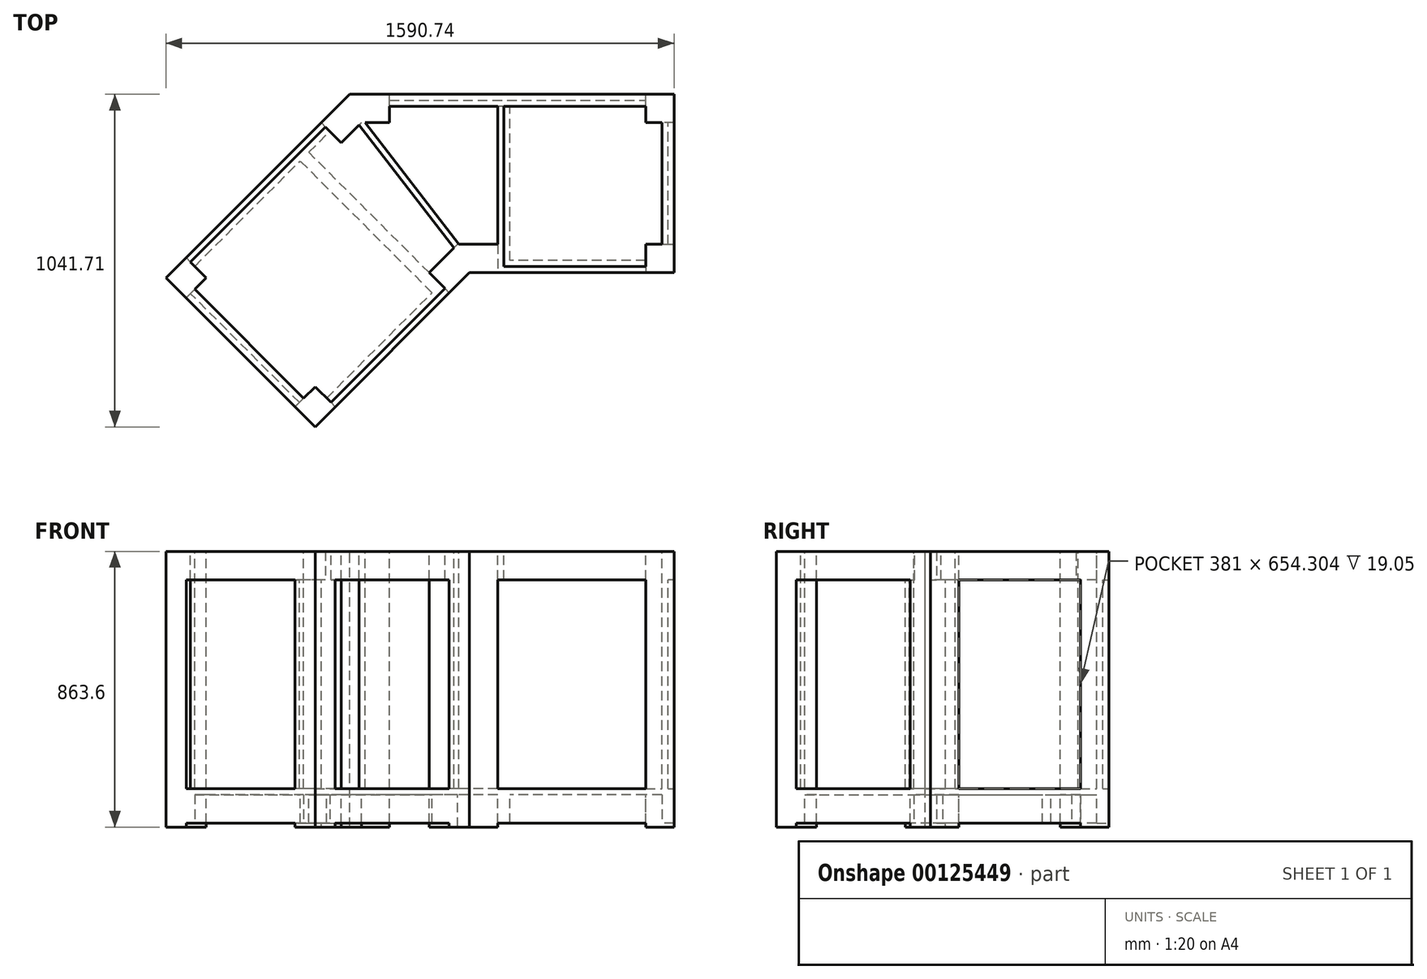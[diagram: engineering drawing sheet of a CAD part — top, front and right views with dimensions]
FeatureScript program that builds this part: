
annotation { "Feature Type Name" : "Feature", "Feature Type Description" : "" }
export const myFeature = defineFeature(function(context is Context, id is Id, definition is map)
    precondition{}
    {
        {
            var Q0;
            Q0=qCreatedBy(makeId("Top.planeOp"),FACE);
            var sketch = newSketch(context, id + "F0", { "sketchPlane" : qUnion([Q0])});
            skLineSegment(sketch, "E0", {"start": v(0, 0) * mm, "end": v(1016, 0) * mm, "construction": true});
            skLineSegment(sketch, "E1", {"start": v(-574.74, -574.74) * mm, "end": v(0, 0) * mm, "construction": true});
            skLineSegment(sketch, "E2.bottom", {"start": v(-88.9, -88.9) * mm, "end": v(-26.04, -26.04) * mm});
            skLineSegment(sketch, "E2.top", {"start": v(-26.04, -151.76) * mm, "end": v(36.82, -88.9) * mm});
            skLineSegment(sketch, "E2.left", {"start": v(-88.9, -88.9) * mm, "end": v(-26.04, -151.76) * mm});
            skLineSegment(sketch, "E3.bottom", {"start": v(36.82, 0) * mm, "end": v(125.72, 0) * mm});
            skLineSegment(sketch, "E3.top", {"start": v(36.82, -88.9) * mm, "end": v(125.72, -88.9) * mm});
            skLineSegment(sketch, "E3.right", {"start": v(125.72, 0) * mm, "end": v(125.72, -88.9) * mm});
            skLineSegment(sketch, "E4.bottom", {"start": v(-574.74, -574.74) * mm, "end": v(-511.87, -511.87) * mm});
            skLineSegment(sketch, "E4.top", {"start": v(-511.87, -637.6) * mm, "end": v(-449.01, -574.74) * mm});
            skLineSegment(sketch, "E4.left", {"start": v(-574.74, -574.74) * mm, "end": v(-511.87, -637.6) * mm});
            skLineSegment(sketch, "E4.right", {"start": v(-511.87, -511.87) * mm, "end": v(-449.01, -574.74) * mm});
            skLineSegment(sketch, "E5.bottom", {"start": v(927.1, 0) * mm, "end": v(1016, 0) * mm});
            skLineSegment(sketch, "E5.top", {"start": v(927.1, -88.9) * mm, "end": v(1016, -88.9) * mm});
            skLineSegment(sketch, "E5.left", {"start": v(927.1, 0) * mm, "end": v(927.1, -88.9) * mm});
            skLineSegment(sketch, "E5.right", {"start": v(1016, 0) * mm, "end": v(1016, -88.9) * mm});
            skLineSegment(sketch, "E6", {"start": v(-26.04, -26.04) * mm, "end": v(0, 0) * mm});
            skLineSegment(sketch, "E7", {"start": v(36.82, 0) * mm, "end": v(0, 0) * mm});
            skLineSegment(sketch, "E8", {"start": v(-574.74, -574.74) * mm, "end": v(-107.76, -1041.7) * mm, "construction": true});
            skLineSegment(sketch, "E9", {"start": v(-107.76, -1041.7) * mm, "end": v(375.15, -558.8) * mm, "construction": true});
            skLineSegment(sketch, "E10", {"start": v(375.15, -558.8) * mm, "end": v(1016, -558.8) * mm, "construction": true});
            skLineSegment(sketch, "E11", {"start": v(1016, -558.8) * mm, "end": v(1016, 0) * mm, "construction": true});
            skLineSegment(sketch, "E12.bottom", {"start": v(-107.76, -1041.7) * mm, "end": v(-44.9, -978.85) * mm});
            skLineSegment(sketch, "E12.top", {"start": v(-170.62, -978.85) * mm, "end": v(-107.76, -915.99) * mm});
            skLineSegment(sketch, "E12.left", {"start": v(-107.76, -1041.7) * mm, "end": v(-170.62, -978.85) * mm});
            skLineSegment(sketch, "E12.right", {"start": v(-44.9, -978.85) * mm, "end": v(-107.76, -915.99) * mm});
            skLineSegment(sketch, "E13.bottom", {"start": v(1016, -558.8) * mm, "end": v(927.1, -558.8) * mm});
            skLineSegment(sketch, "E13.top", {"start": v(1016, -469.9) * mm, "end": v(927.1, -469.9) * mm});
            skLineSegment(sketch, "E13.left", {"start": v(1016, -558.8) * mm, "end": v(1016, -469.9) * mm});
            skLineSegment(sketch, "E13.right", {"start": v(927.1, -558.8) * mm, "end": v(927.1, -469.9) * mm});
            skLineSegment(sketch, "E14.bottom", {"start": v(375.15, -558.8) * mm, "end": v(464.05, -558.8) * mm});
            skLineSegment(sketch, "E14.top", {"start": v(375.15, -469.9) * mm, "end": v(464.05, -469.9) * mm});
            skLineSegment(sketch, "E14.right", {"start": v(464.05, -558.8) * mm, "end": v(464.05, -469.9) * mm});
            skLineSegment(sketch, "E15.bottom", {"start": v(375.15, -558.8) * mm, "end": v(312.28, -621.66) * mm});
            skLineSegment(sketch, "E15.top", {"start": v(312.28, -495.94) * mm, "end": v(249.42, -558.8) * mm});
            skLineSegment(sketch, "E15.right", {"start": v(312.28, -621.66) * mm, "end": v(249.42, -558.8) * mm});
            skLineSegment(sketch, "E16", {"start": v(312.28, -495.94) * mm, "end": v(338.32, -469.9) * mm});
            skLineSegment(sketch, "E17", {"start": v(375.15, -469.9) * mm, "end": v(338.32, -469.9) * mm});
            skSolve(sketch);
        }
        {
            var Q0;
            Q0=makeQuery(id+"F0.imprint","IMPRINT",FACE,{"disambiguationData":[TD([[makeQuery(id+"F0.imprint","IMPRINT",EDGE,{"derivedFrom":sQuery(id+"F0.wireOp",EDGE,"E2.bottom")}),-1.0]])]});
            var Q1;
            Q1=makeQuery(id+"F0.imprint","IMPRINT",FACE,{"disambiguationData":[TD([[makeQuery(id+"F0.imprint","IMPRINT",EDGE,{"derivedFrom":sQuery(id+"F0.wireOp",EDGE,"E3.bottom")}),-1.0]])]});
            var Q2;
            Q2=makeQuery(id+"F0.imprint","IMPRINT",FACE,{"disambiguationData":[TD([[makeQuery(id+"F0.imprint","IMPRINT",EDGE,{"derivedFrom":sQuery(id+"F0.wireOp",EDGE,"E5.bottom")}),-1.0]])]});
            var Q3;
            Q3=makeQuery(id+"F0.imprint","IMPRINT",FACE,{"disambiguationData":[TD([[makeQuery(id+"F0.imprint","IMPRINT",EDGE,{"derivedFrom":sQuery(id+"F0.wireOp",EDGE,"E4.bottom")}),-1.0]])]});
            var Q4;
            Q4=makeQuery(id+"F0.imprint","IMPRINT",FACE,{"disambiguationData":[TD([[makeQuery(id+"F0.imprint","IMPRINT",EDGE,{"derivedFrom":sQuery(id+"F0.wireOp",EDGE,"E12.bottom")}),1.0]])]});
            var Q5;
            Q5=makeQuery(id+"F0.imprint","IMPRINT",FACE,{"disambiguationData":[TD([[makeQuery(id+"F0.imprint","IMPRINT",EDGE,{"derivedFrom":sQuery(id+"F0.wireOp",EDGE,"E14.bottom")}),1.0]])]});
            var Q6;
            Q6=makeQuery(id+"F0.imprint","IMPRINT",FACE,{"disambiguationData":[TD([[makeQuery(id+"F0.imprint","IMPRINT",EDGE,{"derivedFrom":sQuery(id+"F0.wireOp",EDGE,"E13.bottom")}),-1.0]])]});
            extrude(context, id + "F1", {"entities" : qUnion([Q0, Q1, Q2, Q3, Q4, Q5, Q6]), "oppositeDirection" : true, "depth" : 863.6 * mm});
        }
        {
            var Q0;
            Q0=qCreatedBy(makeId("Top.planeOp"),FACE);
            var sketch = newSketch(context, id + "F2", { "sketchPlane" : qUnion([Q0])});
            skLineSegment(sketch, "E18.bottom", {"start": v(0, 0) * mm, "end": v(1016, 0) * mm});
            skLineSegment(sketch, "E19.MirrorCS", {"start": v(0, 0) * mm, "end": v(-574.74, -574.74) * mm});
            skPoint(sketch, "E20.orphan", {"position": v(0, -25.4) * mm});
            skPoint(sketch, "E21.orphan", {"position": v(8.69, -23.87) * mm});
            skLineSegment(sketch, "E22.bottom", {"start": v(-107.76, -1041.7) * mm, "end": v(375.15, -558.8) * mm});
            skLineSegment(sketch, "E23.bottom", {"start": v(1016, -558.8) * mm, "end": v(375.15, -558.8) * mm});
            skLineSegment(sketch, "E24", {"start": v(-574.74, -574.74) * mm, "end": v(-107.76, -1041.7) * mm});
            skLineSegment(sketch, "E25", {"start": v(1016, 0) * mm, "end": v(1016, -558.8) * mm});
            skLineSegment(sketch, "E26.1", {"start": v(-107.76, -1014.77) * mm, "end": v(367.26, -539.75) * mm});
            skLineSegment(sketch, "E26.2", {"start": v(996.95, -539.75) * mm, "end": v(483.1, -539.75) * mm});
            skLineSegment(sketch, "E26.3", {"start": v(-547.8, -574.74) * mm, "end": v(-107.76, -1014.77) * mm});
            skLineSegment(sketch, "E26.4", {"start": v(996.95, -19.05) * mm, "end": v(996.95, -539.75) * mm});
            skLineSegment(sketch, "E26.5", {"start": v(7.9, -19.05) * mm, "end": v(464.05, -19.05) * mm});
            skLineSegment(sketch, "E27.MirrorCS", {"start": v(483.1, -19.05) * mm, "end": v(483.1, -539.75) * mm});
            skLineSegment(sketch, "E28.MirrorCS", {"start": v(464.05, -19.05) * mm, "end": v(464.05, -539.75) * mm});
            skLineSegment(sketch, "E29.trimOffspring", {"start": v(7.9, -19.05) * mm, "end": v(-547.8, -574.74) * mm});
            skLineSegment(sketch, "E30.trimOffspring", {"start": v(483.1, -19.05) * mm, "end": v(996.95, -19.05) * mm});
            skLineSegment(sketch, "E31.trimOffspring", {"start": v(464.05, -539.75) * mm, "end": v(367.26, -539.75) * mm});
            skSolve(sketch);
        }
        {
            var Q0;
            Q0=makeQuery(id+"F2.imprint","IMPRINT",FACE,{"disambiguationData":[TD([[makeQuery(id+"F2.imprint","IMPRINT",EDGE,{"derivedFrom":sQuery(id+"F2.wireOp",EDGE,"E18.bottom")}),-1.0]])]});
            extrude(context, id + "F3", {"entities" : qUnion([Q0]), "oppositeDirection" : true, "depth" : 88.9 * mm});
        }
        {
            var Q0;
            Q0=makeQuery(id+"F1.opExtrude","SWEPT_BODY",BODY,{"disambiguationData":[OSD([sQuery(id+"F0.wireOp",EDGE,"E3.bottom"),sQuery(id+"F0.wireOp",EDGE,"E3.top"),sQuery(id+"F0.wireOp",EDGE,"E3.left"),sQuery(id+"F0.wireOp",EDGE,"E3.right")])]});
            var Q1;
            Q1=makeQuery(id+"F3.opExtrude","SWEPT_BODY",BODY,{"disambiguationData":[OSD([sQuery(id+"F2.wireOp",EDGE,"E18.bottom"),sQuery(id+"F2.wireOp",EDGE,"E18.top"),sQuery(id+"F2.wireOp",EDGE,"E18.right"),sQuery(id+"F2.wireOp",EDGE,"85fa7ddf-3c67-48b7-9abf-f146a85abdcc0.MirrorCS"),sQuery(id+"F2.wireOp",EDGE,"E19.MirrorCS"),sQuery(id+"F2.wireOp",EDGE,"1de45453-a286-46f3-bc31-238e124999270.MirrorCS")])]});
            var Q2;
            Q2=makeQuery(id+"F1.opExtrude","SWEPT_BODY",BODY,{"disambiguationData":[OSD([sQuery(id+"F0.wireOp",EDGE,"E5.bottom"),sQuery(id+"F0.wireOp",EDGE,"E5.top"),sQuery(id+"F0.wireOp",EDGE,"E5.left"),sQuery(id+"F0.wireOp",EDGE,"E5.right")])]});
            var Q3;
            Q3=makeQuery(id+"F1.opExtrude","SWEPT_BODY",BODY,{"disambiguationData":[OSD([sQuery(id+"F0.wireOp",EDGE,"E4.bottom"),sQuery(id+"F0.wireOp",EDGE,"E4.top"),sQuery(id+"F0.wireOp",EDGE,"E4.left"),sQuery(id+"F0.wireOp",EDGE,"E4.right")])]});
            var Q4;
            Q4=makeQuery(id+"F1.opExtrude","SWEPT_BODY",BODY,{"disambiguationData":[OSD([sQuery(id+"F0.wireOp",EDGE,"E12.bottom"),sQuery(id+"F0.wireOp",EDGE,"E12.top"),sQuery(id+"F0.wireOp",EDGE,"E12.left"),sQuery(id+"F0.wireOp",EDGE,"E12.right")])]});
            var Q5;
            Q5=makeQuery(id+"F1.opExtrude","SWEPT_BODY",BODY,{"disambiguationData":[OSD([sQuery(id+"F0.wireOp",EDGE,"E14.bottom"),sQuery(id+"F0.wireOp",EDGE,"E14.top"),sQuery(id+"F0.wireOp",EDGE,"E14.right"),sQuery(id+"F0.wireOp",EDGE,"E15.bottom"),sQuery(id+"F0.wireOp",EDGE,"E15.top"),sQuery(id+"F0.wireOp",EDGE,"E15.right"),sQuery(id+"F0.wireOp",EDGE,"E16"),sQuery(id+"F0.wireOp",EDGE,"E17")])]});
            var Q6;
            Q6=makeQuery(id+"F1.opExtrude","SWEPT_BODY",BODY,{"disambiguationData":[OSD([sQuery(id+"F0.wireOp",EDGE,"E13.bottom"),sQuery(id+"F0.wireOp",EDGE,"E13.top"),sQuery(id+"F0.wireOp",EDGE,"E13.left"),sQuery(id+"F0.wireOp",EDGE,"E13.right")])]});
            booleanBodies(context, id + "F4", {"operationType" : BooleanOperationType.UNION, "tools" : qUnion([Q0, Q1, Q2, Q3, Q4, Q5, Q6])});
        }
        {
            var Q0;
            Q0=qCreatedBy(makeId("Top.planeOp"),FACE);
            cPlane(context, id + "F5", {"entities" : qUnion([Q0]), "cplaneType" : CPlaneType.OFFSET, "offset" : 762 * mm, "oppositeDirection" : true, "width" : 152.4 * mm, "height" : 152.4 * mm});
        }
        {
            var Q0;
            Q0=qCreatedBy(id+"F5.planeOp",FACE);
            var sketch = newSketch(context, id + "F6", { "sketchPlane" : qUnion([Q0])});
            skLineSegment(sketch, "E32.bottom", {"start": v(0, 0) * mm, "end": v(1016, 0) * mm});
            skLineSegment(sketch, "E32.top", {"start": v(375.15, -558.8) * mm, "end": v(1016, -558.8) * mm});
            skLineSegment(sketch, "E32.right", {"start": v(1016, 0) * mm, "end": v(1016, -558.8) * mm});
            skLineSegment(sketch, "E33.MirrorCS", {"start": v(375.15, -558.8) * mm, "end": v(-107.76, -1041.7) * mm});
            skLineSegment(sketch, "E34.MirrorCS", {"start": v(0, 0) * mm, "end": v(-574.74, -574.74) * mm});
            skLineSegment(sketch, "E35.MirrorCS", {"start": v(-574.74, -574.74) * mm, "end": v(-107.76, -1041.7) * mm});
            skPoint(sketch, "E36.orphan", {"position": v(275.74, -558.8) * mm});
            skPoint(sketch, "E37.orphan", {"position": v(375.15, -558.8) * mm});
            skLineSegment(sketch, "E38.0", {"start": v(15.78, -38.1) * mm, "end": v(-127.75, -181.63) * mm});
            skLineSegment(sketch, "E38.1", {"start": v(359.37, -520.7) * mm, "end": v(285.34, -594.72) * mm});
            skLineSegment(sketch, "E38.2", {"start": v(359.37, -520.7) * mm, "end": v(464.05, -520.7) * mm});
            skLineSegment(sketch, "E38.3", {"start": v(-520.85, -574.74) * mm, "end": v(-107.76, -987.83) * mm});
            skLineSegment(sketch, "E38.4", {"start": v(977.9, -38.1) * mm, "end": v(977.9, -520.7) * mm});
            skLineSegment(sketch, "E38.5", {"start": v(15.78, -38.1) * mm, "end": v(464.05, -38.1) * mm});
            skLineSegment(sketch, "E39", {"start": v(-127.75, -181.63) * mm, "end": v(285.34, -594.72) * mm});
            skLineSegment(sketch, "E40.0", {"start": v(-154.69, -208.57) * mm, "end": v(258.4, -621.66) * mm});
            skLineSegment(sketch, "E41.trimOffspring", {"start": v(-154.69, -208.57) * mm, "end": v(-520.85, -574.74) * mm});
            skLineSegment(sketch, "E42.trimOffspring", {"start": v(258.4, -621.66) * mm, "end": v(-107.76, -987.83) * mm});
            skLineSegment(sketch, "E43.MirrorCS", {"start": v(464.05, -38.1) * mm, "end": v(464.05, -520.7) * mm});
            skLineSegment(sketch, "E44.MirrorCS", {"start": v(502.15, -38.1) * mm, "end": v(502.15, -520.7) * mm});
            skLineSegment(sketch, "E45.trimOffspring", {"start": v(502.15, -38.1) * mm, "end": v(977.9, -38.1) * mm});
            skLineSegment(sketch, "E46.trimOffspring", {"start": v(502.15, -520.7) * mm, "end": v(977.9, -520.7) * mm});
            skSolve(sketch);
        }
        {
            var Q0;
            Q0=makeQuery(id+"F6.imprint","IMPRINT",FACE,{"disambiguationData":[TD([[makeQuery(id+"F6.imprint","IMPRINT",EDGE,{"derivedFrom":sQuery(id+"F6.wireOp",EDGE,"E32.bottom")}),-1.0]])]});
            extrude(context, id + "F7", {"entities" : qUnion([Q0]), "operationType" : NewBodyOperationType.ADD, "oppositeDirection" : true, "depth" : 88.9 * mm});
        }
        {
            var Q0;
            {var subQ0=sQuery(id+"F6.wireOp",EDGE,"E35.MirrorCS");var subQ1=sQuery(id+"F6.wireOp",EDGE,"E38.3");Q0=makeQuery(id+"F7.boolean.opBoolean","SPLIT",FACE,{"disambiguationData":[TD([makeQuery(id+"F1.opExtrude","SWEPT_FACE",FACE,{"disambiguationData":[OSD([sQuery(id+"F0.wireOp",EDGE,"E4.top")])]})])],"derivedFrom":makeQuery(id+"F7.opExtrude","CAP_FACE",FACE,{"disambiguationData":[OSD([sQuery(id+"F6.wireOp",EDGE,"E32.bottom"),sQuery(id+"F6.wireOp",EDGE,"E32.top"),sQuery(id+"F6.wireOp",EDGE,"E32.right"),sQuery(id+"F6.wireOp",EDGE,"E33.MirrorCS"),sQuery(id+"F6.wireOp",EDGE,"E34.MirrorCS"),subQ0,sQuery(id+"F6.wireOp",EDGE,"E38.0"),sQuery(id+"F6.wireOp",EDGE,"E38.1"),sQuery(id+"F6.wireOp",EDGE,"E38.2"),subQ1,sQuery(id+"F6.wireOp",EDGE,"E38.4"),sQuery(id+"F6.wireOp",EDGE,"E38.5"),sQuery(id+"F6.wireOp",EDGE,"E39"),sQuery(id+"F6.wireOp",EDGE,"E40.0"),sQuery(id+"F6.wireOp",EDGE,"E41.trimOffspring"),sQuery(id+"F6.wireOp",EDGE,"E42.trimOffspring"),sQuery(id+"F6.wireOp",EDGE,"E43.MirrorCS"),sQuery(id+"F6.wireOp",EDGE,"E44.MirrorCS"),sQuery(id+"F6.wireOp",EDGE,"E45.trimOffspring"),sQuery(id+"F6.wireOp",EDGE,"E46.trimOffspring")])],"isStart":true})});}
            var sketch = newSketch(context, id + "F8", { "sketchPlane" : qUnion([Q0])});
            skLineSegment(sketch, "E47", {"start": v(-107.76, -1041.7) * mm, "end": v(375.15, -558.8) * mm});
            skLineSegment(sketch, "E48", {"start": v(375.15, -558.8) * mm, "end": v(1016, -558.8) * mm});
            skLineSegment(sketch, "E49", {"start": v(1016, -558.8) * mm, "end": v(1016, 0) * mm});
            skLineSegment(sketch, "E50", {"start": v(1016, 0) * mm, "end": v(0, 0) * mm});
            skLineSegment(sketch, "E51", {"start": v(0, 0) * mm, "end": v(-574.74, -574.74) * mm});
            skLineSegment(sketch, "E52", {"start": v(-574.74, -574.74) * mm, "end": v(-107.76, -1041.7) * mm});
            skSolve(sketch);
        }
        {
            var Q0;
            Q0 = qSketchRegion(id + "F8", true);
            extrude(context, id + "F9", {"entities" : qUnion([Q0]), "operationType" : NewBodyOperationType.ADD, "depth" : 18.8 * mm, "hasSecondDirection" : true, "secondDirectionOppositeDirection" : true, "secondDirectionDepth" : 0.25 * mm});
        }
        {
            var Q0;
            Q0=qCreatedBy(makeId("Top.planeOp"),FACE);
            var sketch = newSketch(context, id + "F10", { "sketchPlane" : qUnion([Q0])});
            skLineSegment(sketch, "E53.bottom", {"start": v(125.72, -19.05) * mm, "end": v(927.1, -19.05) * mm});
            skLineSegment(sketch, "E53.top", {"start": v(125.72, -38.1) * mm, "end": v(927.1, -38.1) * mm});
            skLineSegment(sketch, "E53.left", {"start": v(125.72, -19.05) * mm, "end": v(125.72, -38.1) * mm});
            skLineSegment(sketch, "E53.right", {"start": v(927.1, -19.05) * mm, "end": v(927.1, -38.1) * mm});
            skLineSegment(sketch, "E54.bottom", {"start": v(996.95, -88.9) * mm, "end": v(977.9, -88.9) * mm});
            skLineSegment(sketch, "E54.top", {"start": v(996.95, -469.9) * mm, "end": v(977.9, -469.9) * mm});
            skLineSegment(sketch, "E54.left", {"start": v(996.95, -88.9) * mm, "end": v(996.95, -469.9) * mm});
            skLineSegment(sketch, "E54.right", {"start": v(977.9, -88.9) * mm, "end": v(977.9, -469.9) * mm});
            skLineSegment(sketch, "E55.bottom", {"start": v(29.27, -94.7) * mm, "end": v(44.37, -83.1) * mm});
            skLineSegment(sketch, "E55.top", {"start": v(326.71, -481.51) * mm, "end": v(341.81, -469.9) * mm});
            skLineSegment(sketch, "E55.left", {"start": v(29.27, -94.7) * mm, "end": v(326.71, -481.51) * mm});
            skLineSegment(sketch, "E55.right", {"start": v(44.37, -83.1) * mm, "end": v(341.81, -469.9) * mm});
            skLineSegment(sketch, "E56.bottom", {"start": v(-498.4, -624.13) * mm, "end": v(-484.93, -610.66) * mm});
            skLineSegment(sketch, "E56.top", {"start": v(-157.15, -965.38) * mm, "end": v(-143.68, -951.9) * mm});
            skLineSegment(sketch, "E56.left", {"start": v(-498.4, -624.13) * mm, "end": v(-157.15, -965.38) * mm});
            skLineSegment(sketch, "E56.right", {"start": v(-484.93, -610.66) * mm, "end": v(-143.68, -951.9) * mm});
            skSolve(sketch);
        }
        {
            var Q0;
            Q0 = qSketchRegion(id + "F10", true);
            extrude(context, id + "F11", {"entities" : qUnion([Q0]), "operationType" : NewBodyOperationType.ADD, "endBound" : BoundingType.UP_TO_NEXT, "oppositeDirection" : true, "depth" : 25.4 * mm});
        }
    });
